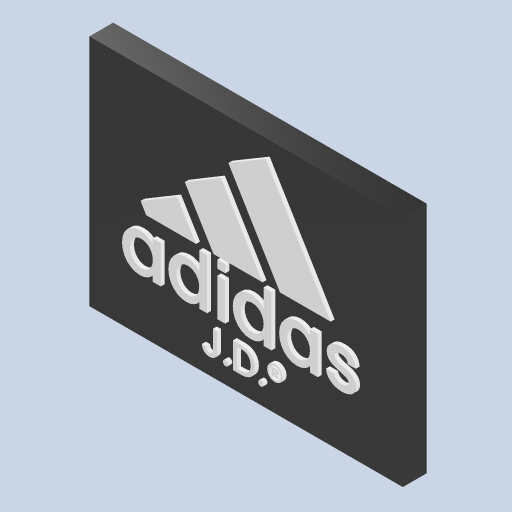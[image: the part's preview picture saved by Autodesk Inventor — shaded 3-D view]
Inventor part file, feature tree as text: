
AUTODESK INVENTOR PART (.ipt)
format: ipt  version: 2023 (Build 270158000, 158)  size: 561,664 bytes
history: native  units: in
note: dims shown in document units (in); Inventor stores cm internally (conversion verified against a paired STEP export)
features: extrude x11, sketch x3, projected_geometry x1
ambient origin geometry x8: Origin, YZ Plane, XZ Plane, XY Plane, X Axis, Y Axis, Z Axis, Center Point
bodies: Solid1 (feature_tree)
feature tree (15):
  sketch  "Sketch1"  dims[d0=9.4488in d1=5.3937in]
  extrude  "Extrusion1"  Depth=5.3937in
  extrude  "Extrusion2"  Depth=1.2205in
  extrude  "Extrusion3"  Depth=2.8346in
  extrude  "Extrusion4"  Depth=3.7008in
  sketch  "Sketch2"  dims[d2=0.4724in d3=1.2205in]
  extrude  "Extrusion5"  Depth=6.2205in
  extrude  "Extrusion6"  Depth=7.2047in
  extrude  "Extrusion7"  Depth=1.063in
  extrude  "Extrusion8"  Depth=1.6929in
  extrude  "Extrusion9"  Depth=4.5669in
  sketch  "Sketch4"  dims[d4=0.3937in d5=2.8346in d6=3.7008in d7=6.2205in d8=7.2047in d9=1.063in d10=1.6929in d11=4.5669in d12=0.2756in d13=2.7559in d14=3.622in d15=6.063in d16=6.9291in d17=0.1969in d18=0.0in d19=0.1969in d20=0.0in d21=0.1969in d22=0.0in d23=0.1969in d24=0.0in d25=0.3929in d26=0.3929in d27=0.1969in d28=0.0in d29=0.1969in d30=0.0in d31=0.1969in d32=0.0in d33=0.1969in d34=0.0in d35=0.1969in d36=0.0in d40=0.1969in d41=0.0in d42=1.1811in d43=0.0in d44=0.1969in d45=0.0344in]
  extrude  "Extrusion11"  Depth=0.2756in
  extrude  "Extrusion12"  Depth=2.7559in
  projected_geometry  "Projected Loop1"
